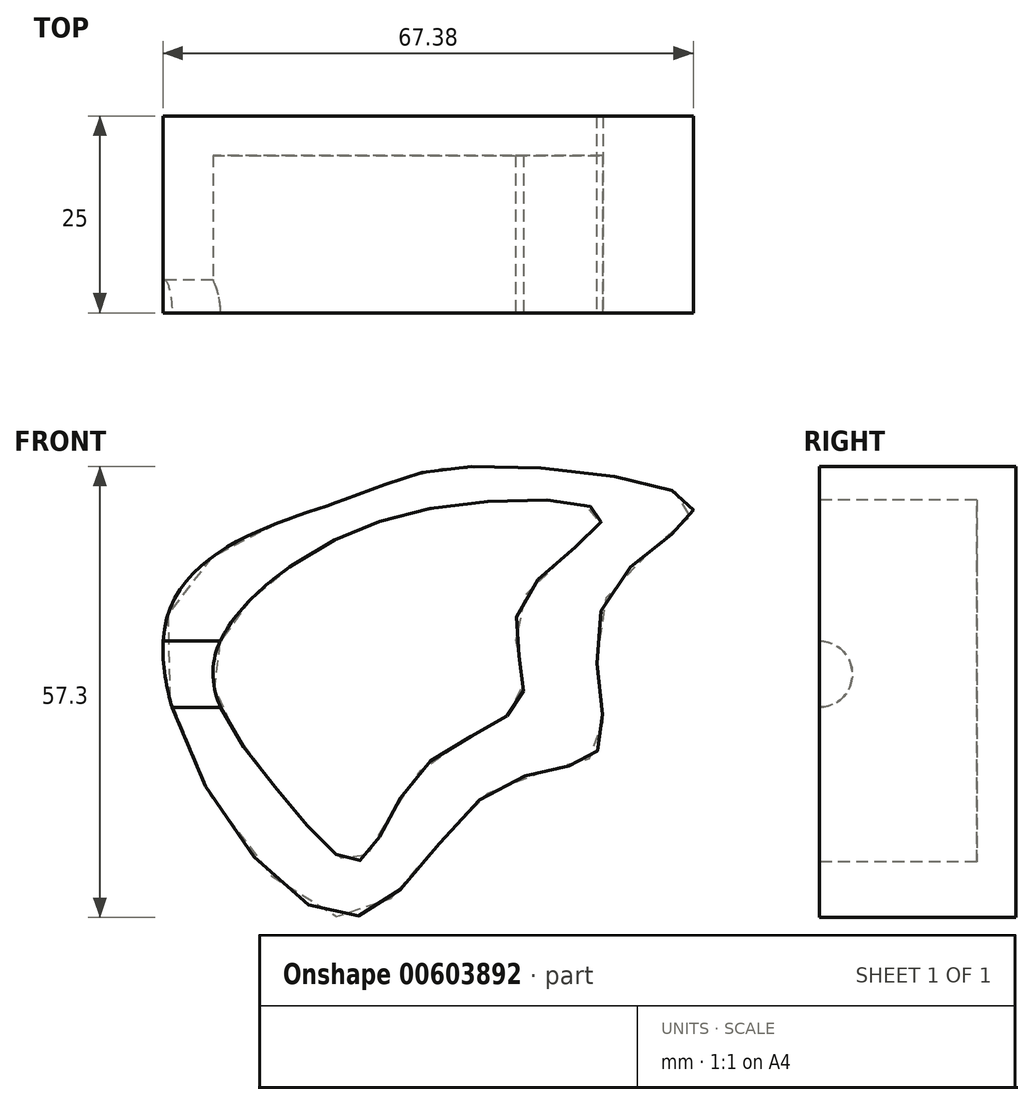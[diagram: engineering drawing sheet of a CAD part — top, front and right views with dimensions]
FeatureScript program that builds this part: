
annotation { "Feature Type Name" : "Feature", "Feature Type Description" : "" }
export const myFeature = defineFeature(function(context is Context, id is Id, definition is map)
    precondition{}
    {
        {
            var Q0;
            Q0=qCreatedBy(makeId("Front.planeOp"),FACE);
            var sketch = newSketch(context, id + "F0", { "sketchPlane" : qUnion([Q0])});
            skFitSpline(sketch, "E0", {"points": [v(-44.26, 63.51) * mm, v(-67.08, 47.49) * mm, v(-44.57, 10.48) * mm, v(-25.58, 26.58) * mm, v(-12, 31.8) * mm, v(-11.15, 50.81) * mm, v(0, 62.67) * mm, v(-28.85, 67.68) * mm, v(-44.26, 63.51) * mm]});
            skSolve(sketch);
        }
        {
            var Q0;
            Q0=makeQuery(id+"F0.imprint","IMPRINT",FACE,{"disambiguationData":[TD([[makeQuery(id+"F0.imprint","IMPRINT",EDGE,{"derivedFrom":sQuery(id+"F0.wireOp",EDGE,"E0")}),1.0]])]});
            extrude(context, id + "F1", {"entities" : qUnion([Q0]), "depth" : 25 * mm, "offsetDistance" : 25 * mm});
        }
        {
            var Q0;
            Q0=makeQuery(id+"F1.opExtrude","CAP_FACE",FACE,{"disambiguationData":[OSD([sQuery(id+"F0.wireOp",EDGE,"E0")])],"isStart":false});
            var sketch = newSketch(context, id + "F2", { "sketchPlane" : qUnion([Q0])});
            skFitSpline(sketch, "E1", {"points": [v(-50.76, 55.3) * mm, v(-61, 41.87) * mm, v(-51.9, 25.55) * mm, v(-42.48, 17.61) * mm, v(-34.36, 29.38) * mm, v(-21.8, 38.18) * mm, v(-22.01, 50.08) * mm, v(-11.53, 61.26) * mm, v(-29.11, 63.02) * mm, v(-50.76, 55.3) * mm]});
            skSolve(sketch);
        }
        {
            var Q0;
            Q0=makeQuery(id+"F2.imprint","IMPRINT",FACE,{"disambiguationData":[TD([[makeQuery(id+"F2.imprint","IMPRINT",EDGE,{"derivedFrom":sQuery(id+"F2.wireOp",EDGE,"E1")}),1.0]])]});
            extrude(context, id + "F3", {"entities" : qUnion([Q0]), "operationType" : NewBodyOperationType.REMOVE, "oppositeDirection" : true, "depth" : 20 * mm, "offsetDistance" : 25 * mm});
        }
        {
            var Q0;
            Q0=makeQuery(id+"F1.opExtrude","CAP_FACE",FACE,{"disambiguationData":[OSD([sQuery(id+"F0.wireOp",EDGE,"E0")])],"isStart":false});
            var sketch = newSketch(context, id + "F4", { "sketchPlane" : qUnion([Q0])});
            skLineSegment(sketch, "E2.bottom", {"start": v(-71.08, 45.56) * mm, "end": v(-57.04, 45.56) * mm});
            skLineSegment(sketch, "E2.top", {"start": v(-71.08, 41.35) * mm, "end": v(-57.04, 41.35) * mm});
            skLineSegment(sketch, "E2.left", {"start": v(-71.08, 45.56) * mm, "end": v(-71.08, 41.35) * mm});
            skLineSegment(sketch, "E2.right", {"start": v(-57.04, 45.56) * mm, "end": v(-57.04, 41.35) * mm});
            skSolve(sketch);
        }
        {
            var Q0;
            {var subQ0=sQuery(id+"F4.wireOp",EDGE,"E2.left");Q0=makeQuery(id+"F4.imprint","IMPRINT",FACE,{"disambiguationData":[TD([[makeQuery(id+"F4.imprint","IMPRINT",EDGE,{"derivedFrom":subQ0}),1.0]])]});}
            var Q1;
            {var subQ0=sQuery(id+"F4.wireOp",EDGE,"E2.bottom");var subQ1=makeQuery(id+"F1.opExtrude","CAP_EDGE",EDGE,{"disambiguationData":[OSD([sQuery(id+"F0.wireOp",EDGE,"E0")])],"isStart":false});var subQ2=makeQuery(id+"F4.imprint","INTERSECT",VERTEX,{"derivedFrom":[subQ1,subQ0]});Q1=makeQuery(id+"F4.imprint","IMPRINT",FACE,{"disambiguationData":[TD([[makeQuery(id+"F4.imprint","IMPRINT",EDGE,{"disambiguationData":[TD([[subQ2,-1.0]])],"derivedFrom":subQ0}),-1.0]])]});}
            var Q2;
            {var subQ0=sQuery(id+"F4.wireOp",EDGE,"E2.right");Q2=makeQuery(id+"F4.imprint","IMPRINT",FACE,{"disambiguationData":[TD([[makeQuery(id+"F4.imprint","IMPRINT",EDGE,{"derivedFrom":subQ0}),-1.0]])]});}
            var Q3;
            Q3=sQuery(id+"F4.wireOp",EDGE,"E2.top");
            revolve(context, id + "F5", {"operationType" : NewBodyOperationType.REMOVE, "entities" : qUnion([Q0, Q1, Q2]), "axis" : qUnion([Q3]), "revolveType" : RevolveType.FULL, "oppositeDirection" : true});
        }
    });
